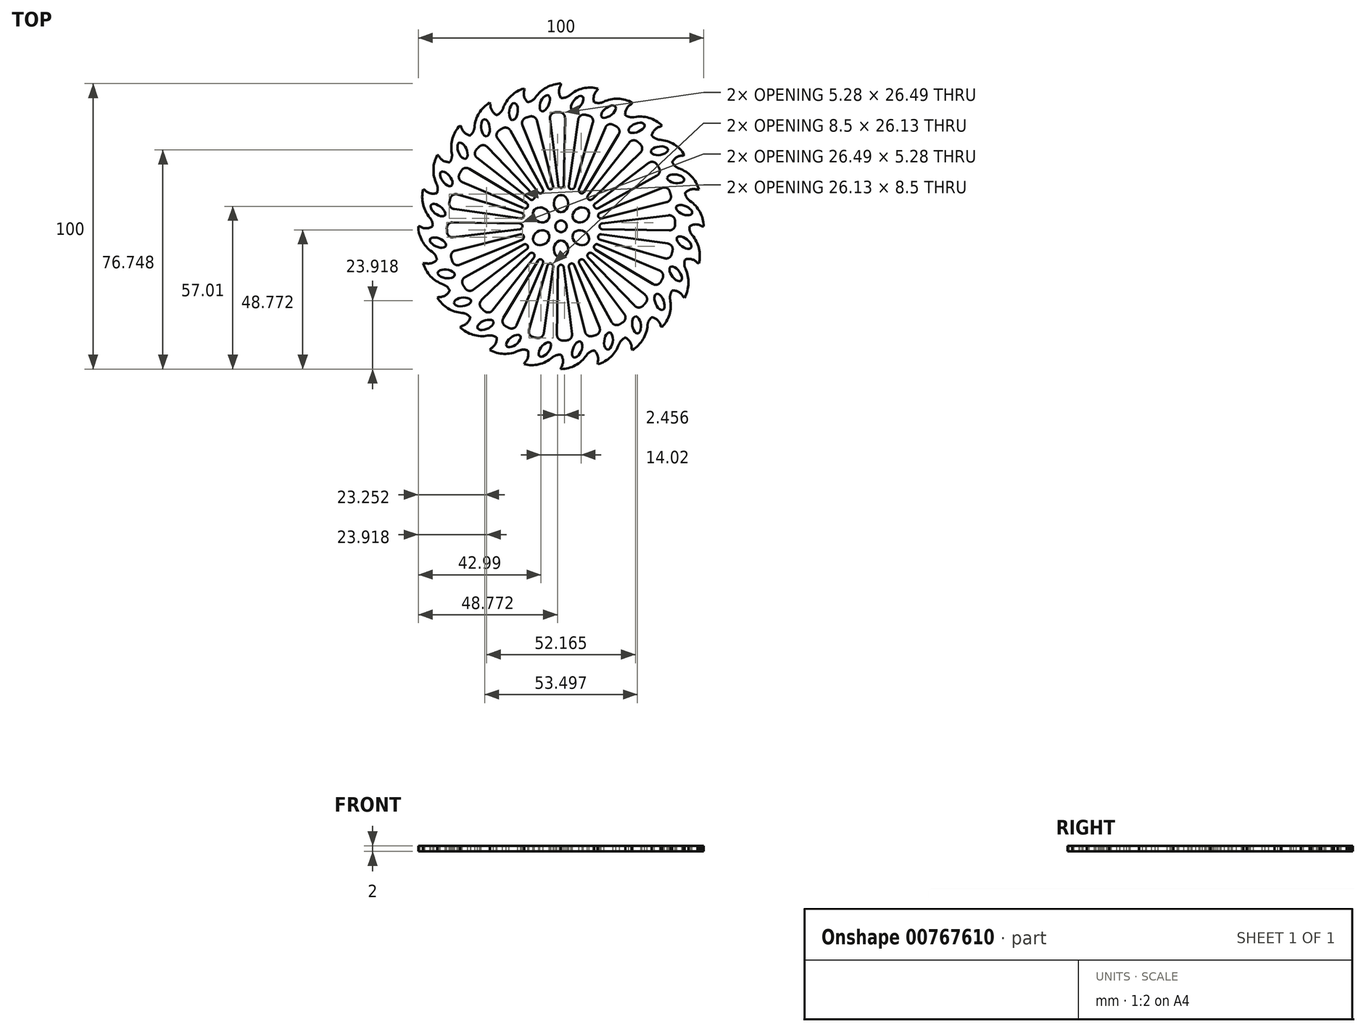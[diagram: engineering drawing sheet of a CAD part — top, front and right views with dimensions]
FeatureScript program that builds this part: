
annotation { "Feature Type Name" : "Feature", "Feature Type Description" : "" }
export const myFeature = defineFeature(function(context is Context, id is Id, definition is map)
    precondition{}
    {
        {
            var Q0;
            Q0=qCreatedBy(makeId("Top.planeOp"),FACE);
            var sketch = newSketch(context, id + "F0", { "sketchPlane" : qUnion([Q0])});
            skCircle(sketch, "E0", {"center": v(0, 0) * mm, "radius": 50 * mm});
            skSolve(sketch);
        }
        {
            var Q0;
            Q0 = qSketchRegion(id + "F0", true);
            extrude(context, id + "F1", {"entities" : qUnion([Q0]), "depth" : 2 * mm, "offsetDistance" : 25 * mm});
        }
        {
            var Q0;
            Q0=qCreatedBy(makeId("Top.planeOp"),FACE);
            var sketch = newSketch(context, id + "F2", { "sketchPlane" : qUnion([Q0])});
            skCircle(sketch, "E1", {"center": v(0, 0) * mm, "radius": 2 * mm});
            skCircle(sketch, "E2", {"center": v(0, 0) * mm, "radius": 45 * mm, "construction": true});
            skLineSegment(sketch, "E3", {"start": v(0, 0) * mm, "end": v(-11.65, 43.47) * mm, "construction": true});
            skArc(sketch, "E4", {"start": v(0, 50) * mm, "mid": v(-5.04, 48.69) * mm, "end": v(-8.91, 45.2) * mm});
            skCircle(sketch, "E5", {"center": v(0, 0) * mm, "radius": 50 * mm, "construction": true});
            skArc(sketch, "E6", {"start": v(-11.65, 43.47) * mm, "mid": v(-11.43, 43.52) * mm, "end": v(-11.22, 43.58) * mm});
            skPoint(sketch, "E7.visualSharp", {"position": v(-9.65, 43.95) * mm});
            skArc(sketch, "E7.filletArc", {"start": v(-11.22, 43.58) * mm, "mid": v(-9.92, 44.18) * mm, "end": v(-8.91, 45.2) * mm});
            skLineSegment(sketch, "E8", {"start": v(0, 50) * mm, "end": v(0, 49.5) * mm});
            skArc(sketch, "E9", {"start": v(0, 49.5) * mm, "mid": v(-0.7, 47.25) * mm, "end": v(0, 45) * mm});
            skArc(sketch, "E10.1.0", {"start": v(-12.94, 48.3) * mm, "mid": v(-17.47, 45.72) * mm, "end": v(-20.3, 41.35) * mm});
            skLineSegment(sketch, "E10.1.1", {"start": v(-12.94, 48.3) * mm, "end": v(-12.81, 47.81) * mm});
            skArc(sketch, "E10.1.2", {"start": v(-12.81, 47.81) * mm, "mid": v(-12.9, 45.46) * mm, "end": v(-11.65, 43.47) * mm});
            skArc(sketch, "E10.1.3", {"start": v(-22.12, 39.19) * mm, "mid": v(-21.02, 40.1) * mm, "end": v(-20.3, 41.35) * mm});
            skArc(sketch, "E10.1.4", {"start": v(-22.5, 38.97) * mm, "mid": v(-22.3, 39.08) * mm, "end": v(-22.12, 39.19) * mm});
            skArc(sketch, "E10.2.0", {"start": v(-25, 43.3) * mm, "mid": v(-28.7, 39.64) * mm, "end": v(-30.32, 34.69) * mm});
            skLineSegment(sketch, "E10.2.1", {"start": v(-25, 43.3) * mm, "end": v(-24.75, 42.87) * mm});
            skArc(sketch, "E10.2.2", {"start": v(-24.75, 42.87) * mm, "mid": v(-24.22, 40.57) * mm, "end": v(-22.5, 38.97) * mm});
            skArc(sketch, "E10.2.3", {"start": v(-31.5, 32.13) * mm, "mid": v(-30.68, 33.3) * mm, "end": v(-30.32, 34.69) * mm});
            skArc(sketch, "E10.2.4", {"start": v(-31.82, 31.82) * mm, "mid": v(-31.66, 31.98) * mm, "end": v(-31.5, 32.13) * mm});
            skArc(sketch, "E10.3.0", {"start": v(-35.36, 35.36) * mm, "mid": v(-38, 30.86) * mm, "end": v(-38.26, 25.66) * mm});
            skLineSegment(sketch, "E10.3.1", {"start": v(-35.36, 35.36) * mm, "end": v(-35, 35) * mm});
            skArc(sketch, "E10.3.2", {"start": v(-35, 35) * mm, "mid": v(-33.9, 32.92) * mm, "end": v(-31.82, 31.82) * mm});
            skArc(sketch, "E10.3.3", {"start": v(-38.75, 22.88) * mm, "mid": v(-38.25, 24.23) * mm, "end": v(-38.26, 25.66) * mm});
            skArc(sketch, "E10.3.4", {"start": v(-38.97, 22.5) * mm, "mid": v(-38.86, 22.7) * mm, "end": v(-38.75, 22.88) * mm});
            skArc(sketch, "E10.4.0", {"start": v(-43.3, 25) * mm, "mid": v(-44.68, 19.98) * mm, "end": v(-43.6, 14.88) * mm});
            skLineSegment(sketch, "E10.4.1", {"start": v(-43.3, 25) * mm, "end": v(-42.87, 24.75) * mm});
            skArc(sketch, "E10.4.2", {"start": v(-42.87, 24.75) * mm, "mid": v(-41.27, 23.03) * mm, "end": v(-38.97, 22.5) * mm});
            skArc(sketch, "E10.4.3", {"start": v(-43.35, 12.07) * mm, "mid": v(-43.22, 13.5) * mm, "end": v(-43.6, 14.88) * mm});
            skArc(sketch, "E10.4.4", {"start": v(-43.47, 11.65) * mm, "mid": v(-43.4, 11.86) * mm, "end": v(-43.35, 12.07) * mm});
            skArc(sketch, "E10.5.0", {"start": v(-48.3, 12.94) * mm, "mid": v(-48.33, 7.73) * mm, "end": v(-45.97, 3.09) * mm});
            skLineSegment(sketch, "E10.5.1", {"start": v(-48.3, 12.94) * mm, "end": v(-47.81, 12.81) * mm});
            skArc(sketch, "E10.5.2", {"start": v(-47.81, 12.81) * mm, "mid": v(-45.82, 11.56) * mm, "end": v(-43.47, 11.65) * mm});
            skArc(sketch, "E10.5.3", {"start": v(-45, 0.44) * mm, "mid": v(-45.24, 1.85) * mm, "end": v(-45.97, 3.09) * mm});
            skArc(sketch, "E10.5.4", {"start": v(-45, 0) * mm, "mid": v(-45, 0.22) * mm, "end": v(-45, 0.44) * mm});
            skArc(sketch, "E10.6.0", {"start": v(-50, 0) * mm, "mid": v(-48.69, -5.04) * mm, "end": v(-45.2, -8.91) * mm});
            skLineSegment(sketch, "E10.6.1", {"start": v(-50, 0) * mm, "end": v(-49.5, 0) * mm});
            skArc(sketch, "E10.6.2", {"start": v(-49.5, 0) * mm, "mid": v(-47.25, -0.7) * mm, "end": v(-45, 0) * mm});
            skArc(sketch, "E10.6.3", {"start": v(-43.58, -11.22) * mm, "mid": v(-44.18, -9.92) * mm, "end": v(-45.2, -8.91) * mm});
            skArc(sketch, "E10.6.4", {"start": v(-43.47, -11.65) * mm, "mid": v(-43.52, -11.43) * mm, "end": v(-43.58, -11.22) * mm});
            skArc(sketch, "E10.7.0", {"start": v(-48.3, -12.94) * mm, "mid": v(-45.72, -17.47) * mm, "end": v(-41.35, -20.3) * mm});
            skLineSegment(sketch, "E10.7.1", {"start": v(-48.3, -12.94) * mm, "end": v(-47.81, -12.81) * mm});
            skArc(sketch, "E10.7.2", {"start": v(-47.81, -12.81) * mm, "mid": v(-45.46, -12.9) * mm, "end": v(-43.47, -11.65) * mm});
            skArc(sketch, "E10.7.3", {"start": v(-39.19, -22.12) * mm, "mid": v(-40.1, -21.02) * mm, "end": v(-41.35, -20.3) * mm});
            skArc(sketch, "E10.7.4", {"start": v(-38.97, -22.5) * mm, "mid": v(-39.08, -22.3) * mm, "end": v(-39.19, -22.12) * mm});
            skArc(sketch, "E10.8.0", {"start": v(-43.3, -25) * mm, "mid": v(-39.64, -28.7) * mm, "end": v(-34.69, -30.32) * mm});
            skLineSegment(sketch, "E10.8.1", {"start": v(-43.3, -25) * mm, "end": v(-42.87, -24.75) * mm});
            skArc(sketch, "E10.8.2", {"start": v(-42.87, -24.75) * mm, "mid": v(-40.57, -24.22) * mm, "end": v(-38.97, -22.5) * mm});
            skArc(sketch, "E10.8.3", {"start": v(-32.13, -31.5) * mm, "mid": v(-33.3, -30.68) * mm, "end": v(-34.69, -30.32) * mm});
            skArc(sketch, "E10.8.4", {"start": v(-31.82, -31.82) * mm, "mid": v(-31.98, -31.66) * mm, "end": v(-32.13, -31.5) * mm});
            skArc(sketch, "E10.9.0", {"start": v(-35.36, -35.36) * mm, "mid": v(-30.86, -38) * mm, "end": v(-25.66, -38.26) * mm});
            skLineSegment(sketch, "E10.9.1", {"start": v(-35.36, -35.36) * mm, "end": v(-35, -35) * mm});
            skArc(sketch, "E10.9.2", {"start": v(-35, -35) * mm, "mid": v(-32.92, -33.9) * mm, "end": v(-31.82, -31.82) * mm});
            skArc(sketch, "E10.9.3", {"start": v(-22.88, -38.75) * mm, "mid": v(-24.23, -38.25) * mm, "end": v(-25.66, -38.26) * mm});
            skArc(sketch, "E10.9.4", {"start": v(-22.5, -38.97) * mm, "mid": v(-22.7, -38.86) * mm, "end": v(-22.88, -38.75) * mm});
            skArc(sketch, "E10.10.0", {"start": v(-25, -43.3) * mm, "mid": v(-19.98, -44.68) * mm, "end": v(-14.88, -43.6) * mm});
            skLineSegment(sketch, "E10.10.1", {"start": v(-25, -43.3) * mm, "end": v(-24.75, -42.87) * mm});
            skArc(sketch, "E10.10.2", {"start": v(-24.75, -42.87) * mm, "mid": v(-23.03, -41.27) * mm, "end": v(-22.5, -38.97) * mm});
            skArc(sketch, "E10.10.3", {"start": v(-12.07, -43.35) * mm, "mid": v(-13.5, -43.22) * mm, "end": v(-14.88, -43.6) * mm});
            skArc(sketch, "E10.10.4", {"start": v(-11.65, -43.47) * mm, "mid": v(-11.86, -43.4) * mm, "end": v(-12.07, -43.35) * mm});
            skArc(sketch, "E10.11.0", {"start": v(-12.94, -48.3) * mm, "mid": v(-7.73, -48.33) * mm, "end": v(-3.09, -45.97) * mm});
            skLineSegment(sketch, "E10.11.1", {"start": v(-12.94, -48.3) * mm, "end": v(-12.81, -47.81) * mm});
            skArc(sketch, "E10.11.2", {"start": v(-12.81, -47.81) * mm, "mid": v(-11.56, -45.82) * mm, "end": v(-11.65, -43.47) * mm});
            skArc(sketch, "E10.11.3", {"start": v(-0.44, -45) * mm, "mid": v(-1.85, -45.24) * mm, "end": v(-3.09, -45.97) * mm});
            skArc(sketch, "E10.11.4", {"start": v(0, -45) * mm, "mid": v(-0.22, -45) * mm, "end": v(-0.44, -45) * mm});
            skArc(sketch, "E10.12.0", {"start": v(0, -50) * mm, "mid": v(5.04, -48.69) * mm, "end": v(8.91, -45.2) * mm});
            skLineSegment(sketch, "E10.12.1", {"start": v(0, -50) * mm, "end": v(0, -49.5) * mm});
            skArc(sketch, "E10.12.2", {"start": v(0, -49.5) * mm, "mid": v(0.7, -47.25) * mm, "end": v(0, -45) * mm});
            skArc(sketch, "E10.12.3", {"start": v(11.22, -43.58) * mm, "mid": v(9.92, -44.18) * mm, "end": v(8.91, -45.2) * mm});
            skArc(sketch, "E10.12.4", {"start": v(11.65, -43.47) * mm, "mid": v(11.43, -43.52) * mm, "end": v(11.22, -43.58) * mm});
            skArc(sketch, "E10.13.0", {"start": v(12.94, -48.3) * mm, "mid": v(17.47, -45.72) * mm, "end": v(20.3, -41.35) * mm});
            skLineSegment(sketch, "E10.13.1", {"start": v(12.94, -48.3) * mm, "end": v(12.81, -47.81) * mm});
            skArc(sketch, "E10.13.2", {"start": v(12.81, -47.81) * mm, "mid": v(12.9, -45.46) * mm, "end": v(11.65, -43.47) * mm});
            skArc(sketch, "E10.13.3", {"start": v(22.12, -39.19) * mm, "mid": v(21.02, -40.1) * mm, "end": v(20.3, -41.35) * mm});
            skArc(sketch, "E10.13.4", {"start": v(22.5, -38.97) * mm, "mid": v(22.3, -39.08) * mm, "end": v(22.12, -39.19) * mm});
            skArc(sketch, "E10.14.0", {"start": v(25, -43.3) * mm, "mid": v(28.7, -39.64) * mm, "end": v(30.32, -34.69) * mm});
            skLineSegment(sketch, "E10.14.1", {"start": v(25, -43.3) * mm, "end": v(24.75, -42.87) * mm});
            skArc(sketch, "E10.14.2", {"start": v(24.75, -42.87) * mm, "mid": v(24.22, -40.57) * mm, "end": v(22.5, -38.97) * mm});
            skArc(sketch, "E10.14.3", {"start": v(31.5, -32.13) * mm, "mid": v(30.68, -33.3) * mm, "end": v(30.32, -34.69) * mm});
            skArc(sketch, "E10.14.4", {"start": v(31.82, -31.82) * mm, "mid": v(31.66, -31.98) * mm, "end": v(31.5, -32.13) * mm});
            skArc(sketch, "E10.15.0", {"start": v(35.36, -35.36) * mm, "mid": v(38, -30.86) * mm, "end": v(38.26, -25.66) * mm});
            skLineSegment(sketch, "E10.15.1", {"start": v(35.36, -35.36) * mm, "end": v(35, -35) * mm});
            skArc(sketch, "E10.15.2", {"start": v(35, -35) * mm, "mid": v(33.9, -32.92) * mm, "end": v(31.82, -31.82) * mm});
            skArc(sketch, "E10.15.3", {"start": v(38.75, -22.88) * mm, "mid": v(38.25, -24.23) * mm, "end": v(38.26, -25.66) * mm});
            skArc(sketch, "E10.15.4", {"start": v(38.97, -22.5) * mm, "mid": v(38.86, -22.7) * mm, "end": v(38.75, -22.88) * mm});
            skArc(sketch, "E10.16.0", {"start": v(43.3, -25) * mm, "mid": v(44.68, -19.98) * mm, "end": v(43.6, -14.88) * mm});
            skLineSegment(sketch, "E10.16.1", {"start": v(43.3, -25) * mm, "end": v(42.87, -24.75) * mm});
            skArc(sketch, "E10.16.2", {"start": v(42.87, -24.75) * mm, "mid": v(41.27, -23.03) * mm, "end": v(38.97, -22.5) * mm});
            skArc(sketch, "E10.16.3", {"start": v(43.35, -12.07) * mm, "mid": v(43.22, -13.5) * mm, "end": v(43.6, -14.88) * mm});
            skArc(sketch, "E10.16.4", {"start": v(43.47, -11.65) * mm, "mid": v(43.4, -11.86) * mm, "end": v(43.35, -12.07) * mm});
            skArc(sketch, "E10.17.0", {"start": v(48.3, -12.94) * mm, "mid": v(48.33, -7.73) * mm, "end": v(45.97, -3.09) * mm});
            skLineSegment(sketch, "E10.17.1", {"start": v(48.3, -12.94) * mm, "end": v(47.81, -12.81) * mm});
            skArc(sketch, "E10.17.2", {"start": v(47.81, -12.81) * mm, "mid": v(45.82, -11.56) * mm, "end": v(43.47, -11.65) * mm});
            skArc(sketch, "E10.17.3", {"start": v(45, -0.44) * mm, "mid": v(45.24, -1.85) * mm, "end": v(45.97, -3.09) * mm});
            skArc(sketch, "E10.17.4", {"start": v(45, 0) * mm, "mid": v(45, -0.22) * mm, "end": v(45, -0.44) * mm});
            skArc(sketch, "E10.18.0", {"start": v(50, 0) * mm, "mid": v(48.69, 5.04) * mm, "end": v(45.2, 8.91) * mm});
            skLineSegment(sketch, "E10.18.1", {"start": v(50, 0) * mm, "end": v(49.5, 0) * mm});
            skArc(sketch, "E10.18.2", {"start": v(49.5, 0) * mm, "mid": v(47.25, 0.7) * mm, "end": v(45, 0) * mm});
            skArc(sketch, "E10.18.3", {"start": v(43.58, 11.22) * mm, "mid": v(44.18, 9.92) * mm, "end": v(45.2, 8.91) * mm});
            skArc(sketch, "E10.18.4", {"start": v(43.47, 11.65) * mm, "mid": v(43.52, 11.43) * mm, "end": v(43.58, 11.22) * mm});
            skArc(sketch, "E10.19.0", {"start": v(48.3, 12.94) * mm, "mid": v(45.72, 17.47) * mm, "end": v(41.35, 20.3) * mm});
            skLineSegment(sketch, "E10.19.1", {"start": v(48.3, 12.94) * mm, "end": v(47.81, 12.81) * mm});
            skArc(sketch, "E10.19.2", {"start": v(47.81, 12.81) * mm, "mid": v(45.46, 12.9) * mm, "end": v(43.47, 11.65) * mm});
            skArc(sketch, "E10.19.3", {"start": v(39.19, 22.12) * mm, "mid": v(40.1, 21.02) * mm, "end": v(41.35, 20.3) * mm});
            skArc(sketch, "E10.19.4", {"start": v(38.97, 22.5) * mm, "mid": v(39.08, 22.3) * mm, "end": v(39.19, 22.12) * mm});
            skArc(sketch, "E10.20.0", {"start": v(43.3, 25) * mm, "mid": v(39.64, 28.7) * mm, "end": v(34.69, 30.32) * mm});
            skLineSegment(sketch, "E10.20.1", {"start": v(43.3, 25) * mm, "end": v(42.87, 24.75) * mm});
            skArc(sketch, "E10.20.2", {"start": v(42.87, 24.75) * mm, "mid": v(40.57, 24.22) * mm, "end": v(38.97, 22.5) * mm});
            skArc(sketch, "E10.20.3", {"start": v(32.13, 31.5) * mm, "mid": v(33.3, 30.68) * mm, "end": v(34.69, 30.32) * mm});
            skArc(sketch, "E10.20.4", {"start": v(31.82, 31.82) * mm, "mid": v(31.98, 31.66) * mm, "end": v(32.13, 31.5) * mm});
            skArc(sketch, "E10.21.0", {"start": v(35.36, 35.36) * mm, "mid": v(30.86, 38) * mm, "end": v(25.66, 38.26) * mm});
            skLineSegment(sketch, "E10.21.1", {"start": v(35.36, 35.36) * mm, "end": v(35, 35) * mm});
            skArc(sketch, "E10.21.2", {"start": v(35, 35) * mm, "mid": v(32.92, 33.9) * mm, "end": v(31.82, 31.82) * mm});
            skArc(sketch, "E10.21.3", {"start": v(22.88, 38.75) * mm, "mid": v(24.23, 38.25) * mm, "end": v(25.66, 38.26) * mm});
            skArc(sketch, "E10.21.4", {"start": v(22.5, 38.97) * mm, "mid": v(22.7, 38.86) * mm, "end": v(22.88, 38.75) * mm});
            skArc(sketch, "E10.22.0", {"start": v(25, 43.3) * mm, "mid": v(19.98, 44.68) * mm, "end": v(14.88, 43.6) * mm});
            skLineSegment(sketch, "E10.22.1", {"start": v(25, 43.3) * mm, "end": v(24.75, 42.87) * mm});
            skArc(sketch, "E10.22.2", {"start": v(24.75, 42.87) * mm, "mid": v(23.03, 41.27) * mm, "end": v(22.5, 38.97) * mm});
            skArc(sketch, "E10.22.3", {"start": v(12.07, 43.35) * mm, "mid": v(13.5, 43.22) * mm, "end": v(14.88, 43.6) * mm});
            skArc(sketch, "E10.22.4", {"start": v(11.65, 43.47) * mm, "mid": v(11.86, 43.4) * mm, "end": v(12.07, 43.35) * mm});
            skArc(sketch, "E10.23.0", {"start": v(12.94, 48.3) * mm, "mid": v(7.73, 48.33) * mm, "end": v(3.09, 45.97) * mm});
            skLineSegment(sketch, "E10.23.1", {"start": v(12.94, 48.3) * mm, "end": v(12.81, 47.81) * mm});
            skArc(sketch, "E10.23.2", {"start": v(12.81, 47.81) * mm, "mid": v(11.56, 45.82) * mm, "end": v(11.65, 43.47) * mm});
            skArc(sketch, "E10.23.3", {"start": v(0.44, 45) * mm, "mid": v(1.85, 45.24) * mm, "end": v(3.09, 45.97) * mm});
            skArc(sketch, "E10.23.4", {"start": v(0, 45) * mm, "mid": v(0.22, 45) * mm, "end": v(0.44, 45) * mm});
            skSolve(sketch);
        }
        {
            var Q0;
            Q0 = qSketchRegion(id + "F2", true);
            extrude(context, id + "F3", {"entities" : qUnion([Q0]), "operationType" : NewBodyOperationType.ADD, "depth" : 4 * mm, "offsetDistance" : 25 * mm});
        }
        {
            var Q0;
            Q0=makeQuery(id+"F1.opExtrude","CAP_FACE",FACE,{"disambiguationData":[OSD([sQuery(id+"F0.wireOp",EDGE,"E0")])],"isStart":true});
            var sketch = newSketch(context, id + "F4", { "sketchPlane" : qUnion([Q0])});
            skCircle(sketch, "E11", {"center": v(0, 0) * mm, "radius": 50 * mm});
            skSolve(sketch);
        }
        {
            var Q0;
            Q0 = qSketchRegion(id + "F4", true);
            extrude(context, id + "F5", {"entities" : qUnion([Q0]), "operationType" : NewBodyOperationType.REMOVE, "oppositeDirection" : true, "depth" : 2 * mm, "offsetDistance" : 25 * mm});
        }
        {
            var Q0;
            Q0=makeQuery(id+"F3.opExtrude","CAP_FACE",FACE,{"disambiguationData":[OSD([sQuery(id+"F2.wireOp",EDGE,"E1"),sQuery(id+"F2.wireOp",EDGE,"E4"),sQuery(id+"F2.wireOp",EDGE,"E8"),sQuery(id+"F2.wireOp",EDGE,"E9"),sQuery(id+"F2.wireOp",EDGE,"E7.filletArc"),sQuery(id+"F2.wireOp",EDGE,"E6"),sQuery(id+"F2.wireOp",EDGE,"E10.1.0"),sQuery(id+"F2.wireOp",EDGE,"E10.1.1"),sQuery(id+"F2.wireOp",EDGE,"E10.1.2"),sQuery(id+"F2.wireOp",EDGE,"E10.1.3"),sQuery(id+"F2.wireOp",EDGE,"E10.1.4"),sQuery(id+"F2.wireOp",EDGE,"E10.2.0"),sQuery(id+"F2.wireOp",EDGE,"E10.2.1"),sQuery(id+"F2.wireOp",EDGE,"E10.2.2"),sQuery(id+"F2.wireOp",EDGE,"E10.2.3"),sQuery(id+"F2.wireOp",EDGE,"E10.2.4"),sQuery(id+"F2.wireOp",EDGE,"E10.3.0"),sQuery(id+"F2.wireOp",EDGE,"E10.3.1"),sQuery(id+"F2.wireOp",EDGE,"E10.3.2"),sQuery(id+"F2.wireOp",EDGE,"E10.3.3"),sQuery(id+"F2.wireOp",EDGE,"E10.3.4"),sQuery(id+"F2.wireOp",EDGE,"E10.4.0"),sQuery(id+"F2.wireOp",EDGE,"E10.4.1"),sQuery(id+"F2.wireOp",EDGE,"E10.4.2"),sQuery(id+"F2.wireOp",EDGE,"E10.4.3"),sQuery(id+"F2.wireOp",EDGE,"E10.4.4"),sQuery(id+"F2.wireOp",EDGE,"E10.5.0"),sQuery(id+"F2.wireOp",EDGE,"E10.5.1"),sQuery(id+"F2.wireOp",EDGE,"E10.5.2"),sQuery(id+"F2.wireOp",EDGE,"E10.5.3"),sQuery(id+"F2.wireOp",EDGE,"E10.5.4"),sQuery(id+"F2.wireOp",EDGE,"E10.6.0"),sQuery(id+"F2.wireOp",EDGE,"E10.6.1"),sQuery(id+"F2.wireOp",EDGE,"E10.6.2"),sQuery(id+"F2.wireOp",EDGE,"E10.6.3"),sQuery(id+"F2.wireOp",EDGE,"E10.6.4"),sQuery(id+"F2.wireOp",EDGE,"E10.7.0"),sQuery(id+"F2.wireOp",EDGE,"E10.7.1"),sQuery(id+"F2.wireOp",EDGE,"E10.7.2"),sQuery(id+"F2.wireOp",EDGE,"E10.7.3"),sQuery(id+"F2.wireOp",EDGE,"E10.7.4"),sQuery(id+"F2.wireOp",EDGE,"E10.8.0"),sQuery(id+"F2.wireOp",EDGE,"E10.8.1"),sQuery(id+"F2.wireOp",EDGE,"E10.8.2"),sQuery(id+"F2.wireOp",EDGE,"E10.8.3"),sQuery(id+"F2.wireOp",EDGE,"E10.8.4"),sQuery(id+"F2.wireOp",EDGE,"E10.9.0"),sQuery(id+"F2.wireOp",EDGE,"E10.9.1"),sQuery(id+"F2.wireOp",EDGE,"E10.9.2"),sQuery(id+"F2.wireOp",EDGE,"E10.9.3"),sQuery(id+"F2.wireOp",EDGE,"E10.9.4"),sQuery(id+"F2.wireOp",EDGE,"E10.10.0"),sQuery(id+"F2.wireOp",EDGE,"E10.10.1"),sQuery(id+"F2.wireOp",EDGE,"E10.10.2"),sQuery(id+"F2.wireOp",EDGE,"E10.10.3"),sQuery(id+"F2.wireOp",EDGE,"E10.10.4"),sQuery(id+"F2.wireOp",EDGE,"E10.11.0"),sQuery(id+"F2.wireOp",EDGE,"E10.11.1"),sQuery(id+"F2.wireOp",EDGE,"E10.11.2"),sQuery(id+"F2.wireOp",EDGE,"E10.11.3"),sQuery(id+"F2.wireOp",EDGE,"E10.11.4"),sQuery(id+"F2.wireOp",EDGE,"E10.12.0"),sQuery(id+"F2.wireOp",EDGE,"E10.12.1"),sQuery(id+"F2.wireOp",EDGE,"E10.12.2"),sQuery(id+"F2.wireOp",EDGE,"E10.12.3"),sQuery(id+"F2.wireOp",EDGE,"E10.12.4"),sQuery(id+"F2.wireOp",EDGE,"E10.13.0"),sQuery(id+"F2.wireOp",EDGE,"E10.13.1"),sQuery(id+"F2.wireOp",EDGE,"E10.13.2"),sQuery(id+"F2.wireOp",EDGE,"E10.13.3"),sQuery(id+"F2.wireOp",EDGE,"E10.13.4"),sQuery(id+"F2.wireOp",EDGE,"E10.14.0"),sQuery(id+"F2.wireOp",EDGE,"E10.14.1"),sQuery(id+"F2.wireOp",EDGE,"E10.14.2"),sQuery(id+"F2.wireOp",EDGE,"E10.14.3"),sQuery(id+"F2.wireOp",EDGE,"E10.14.4"),sQuery(id+"F2.wireOp",EDGE,"E10.15.0"),sQuery(id+"F2.wireOp",EDGE,"E10.15.1"),sQuery(id+"F2.wireOp",EDGE,"E10.15.2"),sQuery(id+"F2.wireOp",EDGE,"E10.15.3"),sQuery(id+"F2.wireOp",EDGE,"E10.15.4"),sQuery(id+"F2.wireOp",EDGE,"E10.16.0"),sQuery(id+"F2.wireOp",EDGE,"E10.16.1"),sQuery(id+"F2.wireOp",EDGE,"E10.16.2"),sQuery(id+"F2.wireOp",EDGE,"E10.16.3"),sQuery(id+"F2.wireOp",EDGE,"E10.16.4"),sQuery(id+"F2.wireOp",EDGE,"E10.17.0"),sQuery(id+"F2.wireOp",EDGE,"E10.17.1"),sQuery(id+"F2.wireOp",EDGE,"E10.17.2"),sQuery(id+"F2.wireOp",EDGE,"E10.17.3"),sQuery(id+"F2.wireOp",EDGE,"E10.17.4"),sQuery(id+"F2.wireOp",EDGE,"E10.18.0"),sQuery(id+"F2.wireOp",EDGE,"E10.18.1"),sQuery(id+"F2.wireOp",EDGE,"E10.18.2"),sQuery(id+"F2.wireOp",EDGE,"E10.18.3"),sQuery(id+"F2.wireOp",EDGE,"E10.18.4"),sQuery(id+"F2.wireOp",EDGE,"E10.19.0"),sQuery(id+"F2.wireOp",EDGE,"E10.19.1"),sQuery(id+"F2.wireOp",EDGE,"E10.19.2"),sQuery(id+"F2.wireOp",EDGE,"E10.19.3"),sQuery(id+"F2.wireOp",EDGE,"E10.19.4"),sQuery(id+"F2.wireOp",EDGE,"E10.20.0"),sQuery(id+"F2.wireOp",EDGE,"E10.20.1"),sQuery(id+"F2.wireOp",EDGE,"E10.20.2"),sQuery(id+"F2.wireOp",EDGE,"E10.20.3"),sQuery(id+"F2.wireOp",EDGE,"E10.20.4"),sQuery(id+"F2.wireOp",EDGE,"E10.21.0"),sQuery(id+"F2.wireOp",EDGE,"E10.21.1"),sQuery(id+"F2.wireOp",EDGE,"E10.21.2"),sQuery(id+"F2.wireOp",EDGE,"E10.21.3"),sQuery(id+"F2.wireOp",EDGE,"E10.21.4"),sQuery(id+"F2.wireOp",EDGE,"E10.22.0"),sQuery(id+"F2.wireOp",EDGE,"E10.22.1"),sQuery(id+"F2.wireOp",EDGE,"E10.22.2"),sQuery(id+"F2.wireOp",EDGE,"E10.22.3"),sQuery(id+"F2.wireOp",EDGE,"E10.22.4"),sQuery(id+"F2.wireOp",EDGE,"E10.23.0"),sQuery(id+"F2.wireOp",EDGE,"E10.23.1"),sQuery(id+"F2.wireOp",EDGE,"E10.23.2"),sQuery(id+"F2.wireOp",EDGE,"E10.23.3"),sQuery(id+"F2.wireOp",EDGE,"E10.23.4")])],"isStart":false});
            var sketch = newSketch(context, id + "F6", { "sketchPlane" : qUnion([Q0])});
            skLineSegment(sketch, "E12", {"start": v(-3.86, 37.71) * mm, "end": v(-1, 14.38) * mm});
            skLineSegment(sketch, "E13", {"start": v(1, 14.48) * mm, "end": v(1.4, 37.96) * mm});
            skArc(sketch, "E14.filletArc", {"start": v(-1, 14.38) * mm, "mid": v(0.05, 13.5) * mm, "end": v(1, 14.48) * mm});
            skPoint(sketch, "E15.visualSharp", {"position": v(-4.25, 40.9) * mm});
            skPoint(sketch, "E16.visualSharp", {"position": v(1.47, 41.18) * mm});
            skArc(sketch, "E17", {"start": v(-1.97, 39.95) * mm, "mid": v(-3.4, 39.24) * mm, "end": v(-3.86, 37.71) * mm});
            skArc(sketch, "E18", {"start": v(1.4, 37.96) * mm, "mid": v(0.83, 39.4) * mm, "end": v(-0.62, 40) * mm});
            skArc(sketch, "E19", {"start": v(-1.97, 39.95) * mm, "mid": v(-1.3, 39.98) * mm, "end": v(-0.62, 40) * mm});
            skArc(sketch, "E20.1.0", {"start": v(-12.24, 38.08) * mm, "mid": v(-13.44, 37.02) * mm, "end": v(-13.49, 35.43) * mm});
            skArc(sketch, "E20.1.1", {"start": v(-12.24, 38.08) * mm, "mid": v(-11.6, 38.28) * mm, "end": v(-10.95, 38.47) * mm});
            skArc(sketch, "E20.1.2", {"start": v(-8.46, 37.03) * mm, "mid": v(-9.4, 38.28) * mm, "end": v(-10.95, 38.47) * mm});
            skLineSegment(sketch, "E20.1.3", {"start": v(-2.78, 14.25) * mm, "end": v(-8.46, 37.03) * mm});
            skLineSegment(sketch, "E20.1.4", {"start": v(-13.49, 35.43) * mm, "end": v(-4.68, 13.63) * mm});
            skArc(sketch, "E20.1.5", {"start": v(-4.68, 13.63) * mm, "mid": v(-3.44, 13.05) * mm, "end": v(-2.78, 14.25) * mm});
            skArc(sketch, "E20.2.0", {"start": v(-21.68, 33.61) * mm, "mid": v(-22.57, 32.28) * mm, "end": v(-22.2, 30.73) * mm});
            skArc(sketch, "E20.2.1", {"start": v(-21.68, 33.61) * mm, "mid": v(-21.11, 33.97) * mm, "end": v(-20.54, 34.33) * mm});
            skArc(sketch, "E20.2.2", {"start": v(-17.76, 33.58) * mm, "mid": v(-18.99, 34.54) * mm, "end": v(-20.54, 34.33) * mm});
            skLineSegment(sketch, "E20.2.3", {"start": v(-6.38, 13.04) * mm, "end": v(-17.76, 33.58) * mm});
            skLineSegment(sketch, "E20.2.4", {"start": v(-22.2, 30.73) * mm, "end": v(-8.05, 11.96) * mm});
            skArc(sketch, "E20.2.5", {"start": v(-8.05, 11.96) * mm, "mid": v(-6.7, 11.72) * mm, "end": v(-6.38, 13.04) * mm});
            skArc(sketch, "E20.3.0", {"start": v(-29.64, 26.86) * mm, "mid": v(-30.15, 25.34) * mm, "end": v(-29.4, 23.94) * mm});
            skArc(sketch, "E20.3.1", {"start": v(-29.64, 26.86) * mm, "mid": v(-29.19, 27.35) * mm, "end": v(-28.72, 27.84) * mm});
            skArc(sketch, "E20.3.2", {"start": v(-25.85, 27.84) * mm, "mid": v(-27.28, 28.45) * mm, "end": v(-28.72, 27.84) * mm});
            skLineSegment(sketch, "E20.3.3", {"start": v(-9.53, 10.95) * mm, "end": v(-25.85, 27.84) * mm});
            skLineSegment(sketch, "E20.3.4", {"start": v(-29.4, 23.94) * mm, "end": v(-10.87, 9.47) * mm});
            skArc(sketch, "E20.3.5", {"start": v(-10.87, 9.47) * mm, "mid": v(-9.5, 9.58) * mm, "end": v(-9.53, 10.95) * mm});
            skArc(sketch, "E20.4.0", {"start": v(-35.58, 18.27) * mm, "mid": v(-35.69, 16.67) * mm, "end": v(-34.59, 15.51) * mm});
            skArc(sketch, "E20.4.1", {"start": v(-35.58, 18.27) * mm, "mid": v(-35.27, 18.87) * mm, "end": v(-34.95, 19.46) * mm});
            skArc(sketch, "E20.4.2", {"start": v(-32.17, 20.2) * mm, "mid": v(-33.72, 20.42) * mm, "end": v(-34.95, 19.46) * mm});
            skLineSegment(sketch, "E20.4.3", {"start": v(-12.04, 8.1) * mm, "end": v(-32.17, 20.2) * mm});
            skLineSegment(sketch, "E20.4.4", {"start": v(-34.59, 15.51) * mm, "end": v(-12.95, 6.33) * mm});
            skArc(sketch, "E20.4.5", {"start": v(-12.95, 6.33) * mm, "mid": v(-11.67, 6.8) * mm, "end": v(-12.04, 8.1) * mm});
            skArc(sketch, "E20.5.0", {"start": v(-39.1, 8.44) * mm, "mid": v(-38.79, 6.87) * mm, "end": v(-37.42, 6.03) * mm});
            skArc(sketch, "E20.5.1", {"start": v(-39.1, 8.44) * mm, "mid": v(-38.95, 9.1) * mm, "end": v(-38.8, 9.75) * mm});
            skArc(sketch, "E20.5.2", {"start": v(-36.3, 11.19) * mm, "mid": v(-37.85, 11) * mm, "end": v(-38.8, 9.75) * mm});
            skLineSegment(sketch, "E20.5.3", {"start": v(-13.73, 4.71) * mm, "end": v(-36.3, 11.19) * mm});
            skLineSegment(sketch, "E20.5.4", {"start": v(-37.42, 6.03) * mm, "end": v(-14.15, 2.76) * mm});
            skArc(sketch, "E20.5.5", {"start": v(-14.15, 2.76) * mm, "mid": v(-13.03, 3.54) * mm, "end": v(-13.73, 4.71) * mm});
            skArc(sketch, "E20.6.0", {"start": v(-39.95, -1.97) * mm, "mid": v(-39.24, -3.4) * mm, "end": v(-37.71, -3.86) * mm});
            skArc(sketch, "E20.6.1", {"start": v(-39.95, -1.97) * mm, "mid": v(-39.98, -1.3) * mm, "end": v(-40, -0.62) * mm});
            skArc(sketch, "E20.6.2", {"start": v(-37.96, 1.4) * mm, "mid": v(-39.4, 0.83) * mm, "end": v(-40, -0.62) * mm});
            skLineSegment(sketch, "E20.6.3", {"start": v(-14.48, 1) * mm, "end": v(-37.96, 1.4) * mm});
            skLineSegment(sketch, "E20.6.4", {"start": v(-37.71, -3.86) * mm, "end": v(-14.38, -1) * mm});
            skArc(sketch, "E20.6.5", {"start": v(-14.38, -1) * mm, "mid": v(-13.5, 0.05) * mm, "end": v(-14.48, 1) * mm});
            skArc(sketch, "E20.7.0", {"start": v(-38.08, -12.24) * mm, "mid": v(-37.02, -13.44) * mm, "end": v(-35.43, -13.49) * mm});
            skArc(sketch, "E20.7.1", {"start": v(-38.08, -12.24) * mm, "mid": v(-38.28, -11.6) * mm, "end": v(-38.47, -10.95) * mm});
            skArc(sketch, "E20.7.2", {"start": v(-37.03, -8.46) * mm, "mid": v(-38.28, -9.4) * mm, "end": v(-38.47, -10.95) * mm});
            skLineSegment(sketch, "E20.7.3", {"start": v(-14.25, -2.78) * mm, "end": v(-37.03, -8.46) * mm});
            skLineSegment(sketch, "E20.7.4", {"start": v(-35.43, -13.49) * mm, "end": v(-13.63, -4.68) * mm});
            skArc(sketch, "E20.7.5", {"start": v(-13.63, -4.68) * mm, "mid": v(-13.05, -3.44) * mm, "end": v(-14.25, -2.78) * mm});
            skArc(sketch, "E20.8.0", {"start": v(-33.61, -21.68) * mm, "mid": v(-32.28, -22.57) * mm, "end": v(-30.73, -22.2) * mm});
            skArc(sketch, "E20.8.1", {"start": v(-33.61, -21.68) * mm, "mid": v(-33.97, -21.11) * mm, "end": v(-34.33, -20.54) * mm});
            skArc(sketch, "E20.8.2", {"start": v(-33.58, -17.76) * mm, "mid": v(-34.54, -18.99) * mm, "end": v(-34.33, -20.54) * mm});
            skLineSegment(sketch, "E20.8.3", {"start": v(-13.04, -6.38) * mm, "end": v(-33.58, -17.76) * mm});
            skLineSegment(sketch, "E20.8.4", {"start": v(-30.73, -22.2) * mm, "end": v(-11.96, -8.05) * mm});
            skArc(sketch, "E20.8.5", {"start": v(-11.96, -8.05) * mm, "mid": v(-11.72, -6.7) * mm, "end": v(-13.04, -6.38) * mm});
            skArc(sketch, "E20.9.0", {"start": v(-26.86, -29.64) * mm, "mid": v(-25.34, -30.15) * mm, "end": v(-23.94, -29.4) * mm});
            skArc(sketch, "E20.9.1", {"start": v(-26.86, -29.64) * mm, "mid": v(-27.35, -29.19) * mm, "end": v(-27.84, -28.72) * mm});
            skArc(sketch, "E20.9.2", {"start": v(-27.84, -25.85) * mm, "mid": v(-28.45, -27.28) * mm, "end": v(-27.84, -28.72) * mm});
            skLineSegment(sketch, "E20.9.3", {"start": v(-10.95, -9.53) * mm, "end": v(-27.84, -25.85) * mm});
            skLineSegment(sketch, "E20.9.4", {"start": v(-23.94, -29.4) * mm, "end": v(-9.47, -10.87) * mm});
            skArc(sketch, "E20.9.5", {"start": v(-9.47, -10.87) * mm, "mid": v(-9.58, -9.5) * mm, "end": v(-10.95, -9.53) * mm});
            skArc(sketch, "E20.10.0", {"start": v(-18.27, -35.58) * mm, "mid": v(-16.67, -35.69) * mm, "end": v(-15.51, -34.59) * mm});
            skArc(sketch, "E20.10.1", {"start": v(-18.27, -35.58) * mm, "mid": v(-18.87, -35.27) * mm, "end": v(-19.46, -34.95) * mm});
            skArc(sketch, "E20.10.2", {"start": v(-20.2, -32.17) * mm, "mid": v(-20.42, -33.72) * mm, "end": v(-19.46, -34.95) * mm});
            skLineSegment(sketch, "E20.10.3", {"start": v(-8.1, -12.04) * mm, "end": v(-20.2, -32.17) * mm});
            skLineSegment(sketch, "E20.10.4", {"start": v(-15.51, -34.59) * mm, "end": v(-6.33, -12.95) * mm});
            skArc(sketch, "E20.10.5", {"start": v(-6.33, -12.95) * mm, "mid": v(-6.8, -11.67) * mm, "end": v(-8.1, -12.04) * mm});
            skArc(sketch, "E20.11.0", {"start": v(-8.44, -39.1) * mm, "mid": v(-6.87, -38.79) * mm, "end": v(-6.03, -37.42) * mm});
            skArc(sketch, "E20.11.1", {"start": v(-8.44, -39.1) * mm, "mid": v(-9.1, -38.95) * mm, "end": v(-9.75, -38.8) * mm});
            skArc(sketch, "E20.11.2", {"start": v(-11.19, -36.3) * mm, "mid": v(-11, -37.85) * mm, "end": v(-9.75, -38.8) * mm});
            skLineSegment(sketch, "E20.11.3", {"start": v(-4.71, -13.73) * mm, "end": v(-11.19, -36.3) * mm});
            skLineSegment(sketch, "E20.11.4", {"start": v(-6.03, -37.42) * mm, "end": v(-2.76, -14.15) * mm});
            skArc(sketch, "E20.11.5", {"start": v(-2.76, -14.15) * mm, "mid": v(-3.54, -13.03) * mm, "end": v(-4.71, -13.73) * mm});
            skArc(sketch, "E20.12.0", {"start": v(1.97, -39.95) * mm, "mid": v(3.4, -39.24) * mm, "end": v(3.86, -37.71) * mm});
            skArc(sketch, "E20.12.1", {"start": v(1.97, -39.95) * mm, "mid": v(1.3, -39.98) * mm, "end": v(0.62, -40) * mm});
            skArc(sketch, "E20.12.2", {"start": v(-1.4, -37.96) * mm, "mid": v(-0.83, -39.4) * mm, "end": v(0.62, -40) * mm});
            skLineSegment(sketch, "E20.12.3", {"start": v(-1, -14.48) * mm, "end": v(-1.4, -37.96) * mm});
            skLineSegment(sketch, "E20.12.4", {"start": v(3.86, -37.71) * mm, "end": v(1, -14.38) * mm});
            skArc(sketch, "E20.12.5", {"start": v(1, -14.38) * mm, "mid": v(-0.05, -13.5) * mm, "end": v(-1, -14.48) * mm});
            skArc(sketch, "E20.13.0", {"start": v(12.24, -38.08) * mm, "mid": v(13.44, -37.02) * mm, "end": v(13.49, -35.43) * mm});
            skArc(sketch, "E20.13.1", {"start": v(12.24, -38.08) * mm, "mid": v(11.6, -38.28) * mm, "end": v(10.95, -38.47) * mm});
            skArc(sketch, "E20.13.2", {"start": v(8.46, -37.03) * mm, "mid": v(9.4, -38.28) * mm, "end": v(10.95, -38.47) * mm});
            skLineSegment(sketch, "E20.13.3", {"start": v(2.78, -14.25) * mm, "end": v(8.46, -37.03) * mm});
            skLineSegment(sketch, "E20.13.4", {"start": v(13.49, -35.43) * mm, "end": v(4.68, -13.63) * mm});
            skArc(sketch, "E20.13.5", {"start": v(4.68, -13.63) * mm, "mid": v(3.44, -13.05) * mm, "end": v(2.78, -14.25) * mm});
            skArc(sketch, "E20.14.0", {"start": v(21.68, -33.61) * mm, "mid": v(22.57, -32.28) * mm, "end": v(22.2, -30.73) * mm});
            skArc(sketch, "E20.14.1", {"start": v(21.68, -33.61) * mm, "mid": v(21.11, -33.97) * mm, "end": v(20.54, -34.33) * mm});
            skArc(sketch, "E20.14.2", {"start": v(17.76, -33.58) * mm, "mid": v(18.99, -34.54) * mm, "end": v(20.54, -34.33) * mm});
            skLineSegment(sketch, "E20.14.3", {"start": v(6.38, -13.04) * mm, "end": v(17.76, -33.58) * mm});
            skLineSegment(sketch, "E20.14.4", {"start": v(22.2, -30.73) * mm, "end": v(8.05, -11.96) * mm});
            skArc(sketch, "E20.14.5", {"start": v(8.05, -11.96) * mm, "mid": v(6.7, -11.72) * mm, "end": v(6.38, -13.04) * mm});
            skArc(sketch, "E20.15.0", {"start": v(29.64, -26.86) * mm, "mid": v(30.15, -25.34) * mm, "end": v(29.4, -23.94) * mm});
            skArc(sketch, "E20.15.1", {"start": v(29.64, -26.86) * mm, "mid": v(29.19, -27.35) * mm, "end": v(28.72, -27.84) * mm});
            skArc(sketch, "E20.15.2", {"start": v(25.85, -27.84) * mm, "mid": v(27.28, -28.45) * mm, "end": v(28.72, -27.84) * mm});
            skLineSegment(sketch, "E20.15.3", {"start": v(9.53, -10.95) * mm, "end": v(25.85, -27.84) * mm});
            skLineSegment(sketch, "E20.15.4", {"start": v(29.4, -23.94) * mm, "end": v(10.87, -9.47) * mm});
            skArc(sketch, "E20.15.5", {"start": v(10.87, -9.47) * mm, "mid": v(9.5, -9.58) * mm, "end": v(9.53, -10.95) * mm});
            skArc(sketch, "E20.16.0", {"start": v(35.58, -18.27) * mm, "mid": v(35.69, -16.67) * mm, "end": v(34.59, -15.51) * mm});
            skArc(sketch, "E20.16.1", {"start": v(35.58, -18.27) * mm, "mid": v(35.27, -18.87) * mm, "end": v(34.95, -19.46) * mm});
            skArc(sketch, "E20.16.2", {"start": v(32.17, -20.2) * mm, "mid": v(33.72, -20.42) * mm, "end": v(34.95, -19.46) * mm});
            skLineSegment(sketch, "E20.16.3", {"start": v(12.04, -8.1) * mm, "end": v(32.17, -20.2) * mm});
            skLineSegment(sketch, "E20.16.4", {"start": v(34.59, -15.51) * mm, "end": v(12.95, -6.33) * mm});
            skArc(sketch, "E20.16.5", {"start": v(12.95, -6.33) * mm, "mid": v(11.67, -6.8) * mm, "end": v(12.04, -8.1) * mm});
            skArc(sketch, "E20.17.0", {"start": v(39.1, -8.44) * mm, "mid": v(38.79, -6.87) * mm, "end": v(37.42, -6.03) * mm});
            skArc(sketch, "E20.17.1", {"start": v(39.1, -8.44) * mm, "mid": v(38.95, -9.1) * mm, "end": v(38.8, -9.75) * mm});
            skArc(sketch, "E20.17.2", {"start": v(36.3, -11.19) * mm, "mid": v(37.85, -11) * mm, "end": v(38.8, -9.75) * mm});
            skLineSegment(sketch, "E20.17.3", {"start": v(13.73, -4.71) * mm, "end": v(36.3, -11.19) * mm});
            skLineSegment(sketch, "E20.17.4", {"start": v(37.42, -6.03) * mm, "end": v(14.15, -2.76) * mm});
            skArc(sketch, "E20.17.5", {"start": v(14.15, -2.76) * mm, "mid": v(13.03, -3.54) * mm, "end": v(13.73, -4.71) * mm});
            skArc(sketch, "E20.18.0", {"start": v(39.95, 1.97) * mm, "mid": v(39.24, 3.4) * mm, "end": v(37.71, 3.86) * mm});
            skArc(sketch, "E20.18.1", {"start": v(39.95, 1.97) * mm, "mid": v(39.98, 1.3) * mm, "end": v(40, 0.62) * mm});
            skArc(sketch, "E20.18.2", {"start": v(37.96, -1.4) * mm, "mid": v(39.4, -0.83) * mm, "end": v(40, 0.62) * mm});
            skLineSegment(sketch, "E20.18.3", {"start": v(14.48, -1) * mm, "end": v(37.96, -1.4) * mm});
            skLineSegment(sketch, "E20.18.4", {"start": v(37.71, 3.86) * mm, "end": v(14.38, 1) * mm});
            skArc(sketch, "E20.18.5", {"start": v(14.38, 1) * mm, "mid": v(13.5, -0.05) * mm, "end": v(14.48, -1) * mm});
            skArc(sketch, "E20.19.0", {"start": v(38.08, 12.24) * mm, "mid": v(37.02, 13.44) * mm, "end": v(35.43, 13.49) * mm});
            skArc(sketch, "E20.19.1", {"start": v(38.08, 12.24) * mm, "mid": v(38.28, 11.6) * mm, "end": v(38.47, 10.95) * mm});
            skArc(sketch, "E20.19.2", {"start": v(37.03, 8.46) * mm, "mid": v(38.28, 9.4) * mm, "end": v(38.47, 10.95) * mm});
            skLineSegment(sketch, "E20.19.3", {"start": v(14.25, 2.78) * mm, "end": v(37.03, 8.46) * mm});
            skLineSegment(sketch, "E20.19.4", {"start": v(35.43, 13.49) * mm, "end": v(13.63, 4.68) * mm});
            skArc(sketch, "E20.19.5", {"start": v(13.63, 4.68) * mm, "mid": v(13.05, 3.44) * mm, "end": v(14.25, 2.78) * mm});
            skArc(sketch, "E20.20.0", {"start": v(33.61, 21.68) * mm, "mid": v(32.28, 22.57) * mm, "end": v(30.73, 22.2) * mm});
            skArc(sketch, "E20.20.1", {"start": v(33.61, 21.68) * mm, "mid": v(33.97, 21.11) * mm, "end": v(34.33, 20.54) * mm});
            skArc(sketch, "E20.20.2", {"start": v(33.58, 17.76) * mm, "mid": v(34.54, 18.99) * mm, "end": v(34.33, 20.54) * mm});
            skLineSegment(sketch, "E20.20.3", {"start": v(13.04, 6.38) * mm, "end": v(33.58, 17.76) * mm});
            skLineSegment(sketch, "E20.20.4", {"start": v(30.73, 22.2) * mm, "end": v(11.96, 8.05) * mm});
            skArc(sketch, "E20.20.5", {"start": v(11.96, 8.05) * mm, "mid": v(11.72, 6.7) * mm, "end": v(13.04, 6.38) * mm});
            skArc(sketch, "E20.21.0", {"start": v(26.86, 29.64) * mm, "mid": v(25.34, 30.15) * mm, "end": v(23.94, 29.4) * mm});
            skArc(sketch, "E20.21.1", {"start": v(26.86, 29.64) * mm, "mid": v(27.35, 29.19) * mm, "end": v(27.84, 28.72) * mm});
            skArc(sketch, "E20.21.2", {"start": v(27.84, 25.85) * mm, "mid": v(28.45, 27.28) * mm, "end": v(27.84, 28.72) * mm});
            skLineSegment(sketch, "E20.21.3", {"start": v(10.95, 9.53) * mm, "end": v(27.84, 25.85) * mm});
            skLineSegment(sketch, "E20.21.4", {"start": v(23.94, 29.4) * mm, "end": v(9.47, 10.87) * mm});
            skArc(sketch, "E20.21.5", {"start": v(9.47, 10.87) * mm, "mid": v(9.58, 9.5) * mm, "end": v(10.95, 9.53) * mm});
            skArc(sketch, "E20.22.0", {"start": v(18.27, 35.58) * mm, "mid": v(16.67, 35.69) * mm, "end": v(15.51, 34.59) * mm});
            skArc(sketch, "E20.22.1", {"start": v(18.27, 35.58) * mm, "mid": v(18.87, 35.27) * mm, "end": v(19.46, 34.95) * mm});
            skArc(sketch, "E20.22.2", {"start": v(20.2, 32.17) * mm, "mid": v(20.42, 33.72) * mm, "end": v(19.46, 34.95) * mm});
            skLineSegment(sketch, "E20.22.3", {"start": v(8.1, 12.04) * mm, "end": v(20.2, 32.17) * mm});
            skLineSegment(sketch, "E20.22.4", {"start": v(15.51, 34.59) * mm, "end": v(6.33, 12.95) * mm});
            skArc(sketch, "E20.22.5", {"start": v(6.33, 12.95) * mm, "mid": v(6.8, 11.67) * mm, "end": v(8.1, 12.04) * mm});
            skArc(sketch, "E20.23.0", {"start": v(8.44, 39.1) * mm, "mid": v(6.87, 38.79) * mm, "end": v(6.03, 37.42) * mm});
            skArc(sketch, "E20.23.1", {"start": v(8.44, 39.1) * mm, "mid": v(9.1, 38.95) * mm, "end": v(9.75, 38.8) * mm});
            skArc(sketch, "E20.23.2", {"start": v(11.19, 36.3) * mm, "mid": v(11, 37.85) * mm, "end": v(9.75, 38.8) * mm});
            skLineSegment(sketch, "E20.23.3", {"start": v(4.71, 13.73) * mm, "end": v(11.19, 36.3) * mm});
            skLineSegment(sketch, "E20.23.4", {"start": v(6.03, 37.42) * mm, "end": v(2.76, 14.15) * mm});
            skArc(sketch, "E20.23.5", {"start": v(2.76, 14.15) * mm, "mid": v(3.54, 13.03) * mm, "end": v(4.71, 13.73) * mm});
            skSolve(sketch);
        }
        {
            var Q0;
            Q0 = qSketchRegion(id + "F6", true);
            extrude(context, id + "F7", {"entities" : qUnion([Q0]), "operationType" : NewBodyOperationType.REMOVE, "oppositeDirection" : true, "depth" : 25 * mm, "offsetDistance" : 25 * mm});
        }
        {
            var Q0;
            Q0=makeQuery(id+"F3.opExtrude","CAP_FACE",FACE,{"disambiguationData":[OSD([sQuery(id+"F2.wireOp",EDGE,"E1"),sQuery(id+"F2.wireOp",EDGE,"E4"),sQuery(id+"F2.wireOp",EDGE,"E8"),sQuery(id+"F2.wireOp",EDGE,"E9"),sQuery(id+"F2.wireOp",EDGE,"E7.filletArc"),sQuery(id+"F2.wireOp",EDGE,"E6"),sQuery(id+"F2.wireOp",EDGE,"E10.1.0"),sQuery(id+"F2.wireOp",EDGE,"E10.1.1"),sQuery(id+"F2.wireOp",EDGE,"E10.1.2"),sQuery(id+"F2.wireOp",EDGE,"E10.1.3"),sQuery(id+"F2.wireOp",EDGE,"E10.1.4"),sQuery(id+"F2.wireOp",EDGE,"E10.2.0"),sQuery(id+"F2.wireOp",EDGE,"E10.2.1"),sQuery(id+"F2.wireOp",EDGE,"E10.2.2"),sQuery(id+"F2.wireOp",EDGE,"E10.2.3"),sQuery(id+"F2.wireOp",EDGE,"E10.2.4"),sQuery(id+"F2.wireOp",EDGE,"E10.3.0"),sQuery(id+"F2.wireOp",EDGE,"E10.3.1"),sQuery(id+"F2.wireOp",EDGE,"E10.3.2"),sQuery(id+"F2.wireOp",EDGE,"E10.3.3"),sQuery(id+"F2.wireOp",EDGE,"E10.3.4"),sQuery(id+"F2.wireOp",EDGE,"E10.4.0"),sQuery(id+"F2.wireOp",EDGE,"E10.4.1"),sQuery(id+"F2.wireOp",EDGE,"E10.4.2"),sQuery(id+"F2.wireOp",EDGE,"E10.4.3"),sQuery(id+"F2.wireOp",EDGE,"E10.4.4"),sQuery(id+"F2.wireOp",EDGE,"E10.5.0"),sQuery(id+"F2.wireOp",EDGE,"E10.5.1"),sQuery(id+"F2.wireOp",EDGE,"E10.5.2"),sQuery(id+"F2.wireOp",EDGE,"E10.5.3"),sQuery(id+"F2.wireOp",EDGE,"E10.5.4"),sQuery(id+"F2.wireOp",EDGE,"E10.6.0"),sQuery(id+"F2.wireOp",EDGE,"E10.6.1"),sQuery(id+"F2.wireOp",EDGE,"E10.6.2"),sQuery(id+"F2.wireOp",EDGE,"E10.6.3"),sQuery(id+"F2.wireOp",EDGE,"E10.6.4"),sQuery(id+"F2.wireOp",EDGE,"E10.7.0"),sQuery(id+"F2.wireOp",EDGE,"E10.7.1"),sQuery(id+"F2.wireOp",EDGE,"E10.7.2"),sQuery(id+"F2.wireOp",EDGE,"E10.7.3"),sQuery(id+"F2.wireOp",EDGE,"E10.7.4"),sQuery(id+"F2.wireOp",EDGE,"E10.8.0"),sQuery(id+"F2.wireOp",EDGE,"E10.8.1"),sQuery(id+"F2.wireOp",EDGE,"E10.8.2"),sQuery(id+"F2.wireOp",EDGE,"E10.8.3"),sQuery(id+"F2.wireOp",EDGE,"E10.8.4"),sQuery(id+"F2.wireOp",EDGE,"E10.9.0"),sQuery(id+"F2.wireOp",EDGE,"E10.9.1"),sQuery(id+"F2.wireOp",EDGE,"E10.9.2"),sQuery(id+"F2.wireOp",EDGE,"E10.9.3"),sQuery(id+"F2.wireOp",EDGE,"E10.9.4"),sQuery(id+"F2.wireOp",EDGE,"E10.10.0"),sQuery(id+"F2.wireOp",EDGE,"E10.10.1"),sQuery(id+"F2.wireOp",EDGE,"E10.10.2"),sQuery(id+"F2.wireOp",EDGE,"E10.10.3"),sQuery(id+"F2.wireOp",EDGE,"E10.10.4"),sQuery(id+"F2.wireOp",EDGE,"E10.11.0"),sQuery(id+"F2.wireOp",EDGE,"E10.11.1"),sQuery(id+"F2.wireOp",EDGE,"E10.11.2"),sQuery(id+"F2.wireOp",EDGE,"E10.11.3"),sQuery(id+"F2.wireOp",EDGE,"E10.11.4"),sQuery(id+"F2.wireOp",EDGE,"E10.12.0"),sQuery(id+"F2.wireOp",EDGE,"E10.12.1"),sQuery(id+"F2.wireOp",EDGE,"E10.12.2"),sQuery(id+"F2.wireOp",EDGE,"E10.12.3"),sQuery(id+"F2.wireOp",EDGE,"E10.12.4"),sQuery(id+"F2.wireOp",EDGE,"E10.13.0"),sQuery(id+"F2.wireOp",EDGE,"E10.13.1"),sQuery(id+"F2.wireOp",EDGE,"E10.13.2"),sQuery(id+"F2.wireOp",EDGE,"E10.13.3"),sQuery(id+"F2.wireOp",EDGE,"E10.13.4"),sQuery(id+"F2.wireOp",EDGE,"E10.14.0"),sQuery(id+"F2.wireOp",EDGE,"E10.14.1"),sQuery(id+"F2.wireOp",EDGE,"E10.14.2"),sQuery(id+"F2.wireOp",EDGE,"E10.14.3"),sQuery(id+"F2.wireOp",EDGE,"E10.14.4"),sQuery(id+"F2.wireOp",EDGE,"E10.15.0"),sQuery(id+"F2.wireOp",EDGE,"E10.15.1"),sQuery(id+"F2.wireOp",EDGE,"E10.15.2"),sQuery(id+"F2.wireOp",EDGE,"E10.15.3"),sQuery(id+"F2.wireOp",EDGE,"E10.15.4"),sQuery(id+"F2.wireOp",EDGE,"E10.16.0"),sQuery(id+"F2.wireOp",EDGE,"E10.16.1"),sQuery(id+"F2.wireOp",EDGE,"E10.16.2"),sQuery(id+"F2.wireOp",EDGE,"E10.16.3"),sQuery(id+"F2.wireOp",EDGE,"E10.16.4"),sQuery(id+"F2.wireOp",EDGE,"E10.17.0"),sQuery(id+"F2.wireOp",EDGE,"E10.17.1"),sQuery(id+"F2.wireOp",EDGE,"E10.17.2"),sQuery(id+"F2.wireOp",EDGE,"E10.17.3"),sQuery(id+"F2.wireOp",EDGE,"E10.17.4"),sQuery(id+"F2.wireOp",EDGE,"E10.18.0"),sQuery(id+"F2.wireOp",EDGE,"E10.18.1"),sQuery(id+"F2.wireOp",EDGE,"E10.18.2"),sQuery(id+"F2.wireOp",EDGE,"E10.18.3"),sQuery(id+"F2.wireOp",EDGE,"E10.18.4"),sQuery(id+"F2.wireOp",EDGE,"E10.19.0"),sQuery(id+"F2.wireOp",EDGE,"E10.19.1"),sQuery(id+"F2.wireOp",EDGE,"E10.19.2"),sQuery(id+"F2.wireOp",EDGE,"E10.19.3"),sQuery(id+"F2.wireOp",EDGE,"E10.19.4"),sQuery(id+"F2.wireOp",EDGE,"E10.20.0"),sQuery(id+"F2.wireOp",EDGE,"E10.20.1"),sQuery(id+"F2.wireOp",EDGE,"E10.20.2"),sQuery(id+"F2.wireOp",EDGE,"E10.20.3"),sQuery(id+"F2.wireOp",EDGE,"E10.20.4"),sQuery(id+"F2.wireOp",EDGE,"E10.21.0"),sQuery(id+"F2.wireOp",EDGE,"E10.21.1"),sQuery(id+"F2.wireOp",EDGE,"E10.21.2"),sQuery(id+"F2.wireOp",EDGE,"E10.21.3"),sQuery(id+"F2.wireOp",EDGE,"E10.21.4"),sQuery(id+"F2.wireOp",EDGE,"E10.22.0"),sQuery(id+"F2.wireOp",EDGE,"E10.22.1"),sQuery(id+"F2.wireOp",EDGE,"E10.22.2"),sQuery(id+"F2.wireOp",EDGE,"E10.22.3"),sQuery(id+"F2.wireOp",EDGE,"E10.22.4"),sQuery(id+"F2.wireOp",EDGE,"E10.23.0"),sQuery(id+"F2.wireOp",EDGE,"E10.23.1"),sQuery(id+"F2.wireOp",EDGE,"E10.23.2"),sQuery(id+"F2.wireOp",EDGE,"E10.23.3"),sQuery(id+"F2.wireOp",EDGE,"E10.23.4")])],"isStart":false});
            var sketch = newSketch(context, id + "F8", { "sketchPlane" : qUnion([Q0])});
            skEllipse(sketch, "E21", {"center": v(0, 8) * mm, "majorRadius": 3 * mm, "minorRadius": 2.5 * mm, "majorAxis": v(0, -1)});
            skEllipse(sketch, "E22.1.0", {"center": v(-6.93, 4) * mm, "majorRadius": 3 * mm, "minorRadius": 2.5 * mm, "majorAxis": v(0.87, -0.5)});
            skEllipse(sketch, "E22.2.0", {"center": v(-6.93, -4) * mm, "majorRadius": 3 * mm, "minorRadius": 2.5 * mm, "majorAxis": v(0.87, 0.5)});
            skEllipse(sketch, "E22.3.0", {"center": v(0, -8) * mm, "majorRadius": 3 * mm, "minorRadius": 2.5 * mm, "majorAxis": v(0, 1)});
            skEllipse(sketch, "E22.4.0", {"center": v(6.93, -4) * mm, "majorRadius": 3 * mm, "minorRadius": 2.5 * mm, "majorAxis": v(-0.87, 0.5)});
            skEllipse(sketch, "E22.5.0", {"center": v(6.93, 4) * mm, "majorRadius": 3 * mm, "minorRadius": 2.5 * mm, "majorAxis": v(-0.87, -0.5)});
            skPoint(sketch, "E22.center", {"position": v(0, 0) * mm});
            skSolve(sketch);
        }
        {
            var Q0;
            Q0 = qSketchRegion(id + "F8", true);
            extrude(context, id + "F9", {"entities" : qUnion([Q0]), "operationType" : NewBodyOperationType.REMOVE, "oppositeDirection" : true, "depth" : 25 * mm, "offsetDistance" : 25 * mm});
        }
        {
            var Q0;
            Q0=makeQuery(id+"F3.opExtrude","CAP_FACE",FACE,{"disambiguationData":[OSD([sQuery(id+"F2.wireOp",EDGE,"E1"),sQuery(id+"F2.wireOp",EDGE,"E4"),sQuery(id+"F2.wireOp",EDGE,"E8"),sQuery(id+"F2.wireOp",EDGE,"E9"),sQuery(id+"F2.wireOp",EDGE,"E7.filletArc"),sQuery(id+"F2.wireOp",EDGE,"E6"),sQuery(id+"F2.wireOp",EDGE,"E10.1.0"),sQuery(id+"F2.wireOp",EDGE,"E10.1.1"),sQuery(id+"F2.wireOp",EDGE,"E10.1.2"),sQuery(id+"F2.wireOp",EDGE,"E10.1.3"),sQuery(id+"F2.wireOp",EDGE,"E10.1.4"),sQuery(id+"F2.wireOp",EDGE,"E10.2.0"),sQuery(id+"F2.wireOp",EDGE,"E10.2.1"),sQuery(id+"F2.wireOp",EDGE,"E10.2.2"),sQuery(id+"F2.wireOp",EDGE,"E10.2.3"),sQuery(id+"F2.wireOp",EDGE,"E10.2.4"),sQuery(id+"F2.wireOp",EDGE,"E10.3.0"),sQuery(id+"F2.wireOp",EDGE,"E10.3.1"),sQuery(id+"F2.wireOp",EDGE,"E10.3.2"),sQuery(id+"F2.wireOp",EDGE,"E10.3.3"),sQuery(id+"F2.wireOp",EDGE,"E10.3.4"),sQuery(id+"F2.wireOp",EDGE,"E10.4.0"),sQuery(id+"F2.wireOp",EDGE,"E10.4.1"),sQuery(id+"F2.wireOp",EDGE,"E10.4.2"),sQuery(id+"F2.wireOp",EDGE,"E10.4.3"),sQuery(id+"F2.wireOp",EDGE,"E10.4.4"),sQuery(id+"F2.wireOp",EDGE,"E10.5.0"),sQuery(id+"F2.wireOp",EDGE,"E10.5.1"),sQuery(id+"F2.wireOp",EDGE,"E10.5.2"),sQuery(id+"F2.wireOp",EDGE,"E10.5.3"),sQuery(id+"F2.wireOp",EDGE,"E10.5.4"),sQuery(id+"F2.wireOp",EDGE,"E10.6.0"),sQuery(id+"F2.wireOp",EDGE,"E10.6.1"),sQuery(id+"F2.wireOp",EDGE,"E10.6.2"),sQuery(id+"F2.wireOp",EDGE,"E10.6.3"),sQuery(id+"F2.wireOp",EDGE,"E10.6.4"),sQuery(id+"F2.wireOp",EDGE,"E10.7.0"),sQuery(id+"F2.wireOp",EDGE,"E10.7.1"),sQuery(id+"F2.wireOp",EDGE,"E10.7.2"),sQuery(id+"F2.wireOp",EDGE,"E10.7.3"),sQuery(id+"F2.wireOp",EDGE,"E10.7.4"),sQuery(id+"F2.wireOp",EDGE,"E10.8.0"),sQuery(id+"F2.wireOp",EDGE,"E10.8.1"),sQuery(id+"F2.wireOp",EDGE,"E10.8.2"),sQuery(id+"F2.wireOp",EDGE,"E10.8.3"),sQuery(id+"F2.wireOp",EDGE,"E10.8.4"),sQuery(id+"F2.wireOp",EDGE,"E10.9.0"),sQuery(id+"F2.wireOp",EDGE,"E10.9.1"),sQuery(id+"F2.wireOp",EDGE,"E10.9.2"),sQuery(id+"F2.wireOp",EDGE,"E10.9.3"),sQuery(id+"F2.wireOp",EDGE,"E10.9.4"),sQuery(id+"F2.wireOp",EDGE,"E10.10.0"),sQuery(id+"F2.wireOp",EDGE,"E10.10.1"),sQuery(id+"F2.wireOp",EDGE,"E10.10.2"),sQuery(id+"F2.wireOp",EDGE,"E10.10.3"),sQuery(id+"F2.wireOp",EDGE,"E10.10.4"),sQuery(id+"F2.wireOp",EDGE,"E10.11.0"),sQuery(id+"F2.wireOp",EDGE,"E10.11.1"),sQuery(id+"F2.wireOp",EDGE,"E10.11.2"),sQuery(id+"F2.wireOp",EDGE,"E10.11.3"),sQuery(id+"F2.wireOp",EDGE,"E10.11.4"),sQuery(id+"F2.wireOp",EDGE,"E10.12.0"),sQuery(id+"F2.wireOp",EDGE,"E10.12.1"),sQuery(id+"F2.wireOp",EDGE,"E10.12.2"),sQuery(id+"F2.wireOp",EDGE,"E10.12.3"),sQuery(id+"F2.wireOp",EDGE,"E10.12.4"),sQuery(id+"F2.wireOp",EDGE,"E10.13.0"),sQuery(id+"F2.wireOp",EDGE,"E10.13.1"),sQuery(id+"F2.wireOp",EDGE,"E10.13.2"),sQuery(id+"F2.wireOp",EDGE,"E10.13.3"),sQuery(id+"F2.wireOp",EDGE,"E10.13.4"),sQuery(id+"F2.wireOp",EDGE,"E10.14.0"),sQuery(id+"F2.wireOp",EDGE,"E10.14.1"),sQuery(id+"F2.wireOp",EDGE,"E10.14.2"),sQuery(id+"F2.wireOp",EDGE,"E10.14.3"),sQuery(id+"F2.wireOp",EDGE,"E10.14.4"),sQuery(id+"F2.wireOp",EDGE,"E10.15.0"),sQuery(id+"F2.wireOp",EDGE,"E10.15.1"),sQuery(id+"F2.wireOp",EDGE,"E10.15.2"),sQuery(id+"F2.wireOp",EDGE,"E10.15.3"),sQuery(id+"F2.wireOp",EDGE,"E10.15.4"),sQuery(id+"F2.wireOp",EDGE,"E10.16.0"),sQuery(id+"F2.wireOp",EDGE,"E10.16.1"),sQuery(id+"F2.wireOp",EDGE,"E10.16.2"),sQuery(id+"F2.wireOp",EDGE,"E10.16.3"),sQuery(id+"F2.wireOp",EDGE,"E10.16.4"),sQuery(id+"F2.wireOp",EDGE,"E10.17.0"),sQuery(id+"F2.wireOp",EDGE,"E10.17.1"),sQuery(id+"F2.wireOp",EDGE,"E10.17.2"),sQuery(id+"F2.wireOp",EDGE,"E10.17.3"),sQuery(id+"F2.wireOp",EDGE,"E10.17.4"),sQuery(id+"F2.wireOp",EDGE,"E10.18.0"),sQuery(id+"F2.wireOp",EDGE,"E10.18.1"),sQuery(id+"F2.wireOp",EDGE,"E10.18.2"),sQuery(id+"F2.wireOp",EDGE,"E10.18.3"),sQuery(id+"F2.wireOp",EDGE,"E10.18.4"),sQuery(id+"F2.wireOp",EDGE,"E10.19.0"),sQuery(id+"F2.wireOp",EDGE,"E10.19.1"),sQuery(id+"F2.wireOp",EDGE,"E10.19.2"),sQuery(id+"F2.wireOp",EDGE,"E10.19.3"),sQuery(id+"F2.wireOp",EDGE,"E10.19.4"),sQuery(id+"F2.wireOp",EDGE,"E10.20.0"),sQuery(id+"F2.wireOp",EDGE,"E10.20.1"),sQuery(id+"F2.wireOp",EDGE,"E10.20.2"),sQuery(id+"F2.wireOp",EDGE,"E10.20.3"),sQuery(id+"F2.wireOp",EDGE,"E10.20.4"),sQuery(id+"F2.wireOp",EDGE,"E10.21.0"),sQuery(id+"F2.wireOp",EDGE,"E10.21.1"),sQuery(id+"F2.wireOp",EDGE,"E10.21.2"),sQuery(id+"F2.wireOp",EDGE,"E10.21.3"),sQuery(id+"F2.wireOp",EDGE,"E10.21.4"),sQuery(id+"F2.wireOp",EDGE,"E10.22.0"),sQuery(id+"F2.wireOp",EDGE,"E10.22.1"),sQuery(id+"F2.wireOp",EDGE,"E10.22.2"),sQuery(id+"F2.wireOp",EDGE,"E10.22.3"),sQuery(id+"F2.wireOp",EDGE,"E10.22.4"),sQuery(id+"F2.wireOp",EDGE,"E10.23.0"),sQuery(id+"F2.wireOp",EDGE,"E10.23.1"),sQuery(id+"F2.wireOp",EDGE,"E10.23.2"),sQuery(id+"F2.wireOp",EDGE,"E10.23.3"),sQuery(id+"F2.wireOp",EDGE,"E10.23.4")])],"isStart":false});
            var sketch = newSketch(context, id + "F10", { "sketchPlane" : qUnion([Q0])});
            skEllipse(sketch, "E23", {"center": v(-5.68, 43.13) * mm, "majorRadius": 3 * mm, "minorRadius": 1.5 * mm, "majorAxis": v(-0.38, -0.92)});
            skLineSegment(sketch, "E24", {"start": v(0, 0) * mm, "end": v(-5.68, 43.13) * mm, "construction": true});
            skLineSegment(sketch, "E25", {"start": v(-4.53, 45.9) * mm, "end": v(-6.83, 40.36) * mm, "construction": true});
            skEllipse(sketch, "E26.1.0", {"center": v(-16.65, 40.19) * mm, "majorRadius": 3 * mm, "minorRadius": 1.5 * mm, "majorAxis": v(-0.13, -1)});
            skEllipse(sketch, "E26.2.0", {"center": v(-26.48, 34.51) * mm, "majorRadius": 3 * mm, "minorRadius": 1.5 * mm, "majorAxis": v(0.13, -1)});
            skEllipse(sketch, "E26.3.0", {"center": v(-34.51, 26.48) * mm, "majorRadius": 3 * mm, "minorRadius": 1.5 * mm, "majorAxis": v(0.38, -0.92)});
            skEllipse(sketch, "E26.4.0", {"center": v(-40.19, 16.65) * mm, "majorRadius": 3 * mm, "minorRadius": 1.5 * mm, "majorAxis": v(0.6, -0.8)});
            skEllipse(sketch, "E26.5.0", {"center": v(-43.13, 5.68) * mm, "majorRadius": 3 * mm, "minorRadius": 1.5 * mm, "majorAxis": v(0.8, -0.6)});
            skEllipse(sketch, "E26.6.0", {"center": v(-43.13, -5.68) * mm, "majorRadius": 3 * mm, "minorRadius": 1.5 * mm, "majorAxis": v(0.92, -0.38)});
            skEllipse(sketch, "E26.7.0", {"center": v(-40.19, -16.65) * mm, "majorRadius": 3 * mm, "minorRadius": 1.5 * mm, "majorAxis": v(1, -0.13)});
            skEllipse(sketch, "E26.8.0", {"center": v(-34.51, -26.48) * mm, "majorRadius": 3 * mm, "minorRadius": 1.5 * mm, "majorAxis": v(1, 0.13)});
            skEllipse(sketch, "E26.9.0", {"center": v(-26.48, -34.51) * mm, "majorRadius": 3 * mm, "minorRadius": 1.5 * mm, "majorAxis": v(0.92, 0.38)});
            skEllipse(sketch, "E26.10.0", {"center": v(-16.65, -40.19) * mm, "majorRadius": 3 * mm, "minorRadius": 1.5 * mm, "majorAxis": v(0.8, 0.6)});
            skEllipse(sketch, "E26.11.0", {"center": v(-5.68, -43.13) * mm, "majorRadius": 3 * mm, "minorRadius": 1.5 * mm, "majorAxis": v(0.6, 0.8)});
            skEllipse(sketch, "E26.12.0", {"center": v(5.68, -43.13) * mm, "majorRadius": 3 * mm, "minorRadius": 1.5 * mm, "majorAxis": v(0.38, 0.92)});
            skEllipse(sketch, "E26.13.0", {"center": v(16.65, -40.19) * mm, "majorRadius": 3 * mm, "minorRadius": 1.5 * mm, "majorAxis": v(0.13, 1)});
            skEllipse(sketch, "E26.14.0", {"center": v(26.48, -34.51) * mm, "majorRadius": 3 * mm, "minorRadius": 1.5 * mm, "majorAxis": v(-0.13, 1)});
            skEllipse(sketch, "E26.15.0", {"center": v(34.51, -26.48) * mm, "majorRadius": 3 * mm, "minorRadius": 1.5 * mm, "majorAxis": v(-0.38, 0.92)});
            skEllipse(sketch, "E26.16.0", {"center": v(40.19, -16.65) * mm, "majorRadius": 3 * mm, "minorRadius": 1.5 * mm, "majorAxis": v(-0.6, 0.8)});
            skEllipse(sketch, "E26.17.0", {"center": v(43.13, -5.68) * mm, "majorRadius": 3 * mm, "minorRadius": 1.5 * mm, "majorAxis": v(-0.8, 0.6)});
            skEllipse(sketch, "E26.18.0", {"center": v(43.13, 5.68) * mm, "majorRadius": 3 * mm, "minorRadius": 1.5 * mm, "majorAxis": v(-0.92, 0.38)});
            skEllipse(sketch, "E26.19.0", {"center": v(40.19, 16.65) * mm, "majorRadius": 3 * mm, "minorRadius": 1.5 * mm, "majorAxis": v(-1, 0.13)});
            skEllipse(sketch, "E26.20.0", {"center": v(34.51, 26.48) * mm, "majorRadius": 3 * mm, "minorRadius": 1.5 * mm, "majorAxis": v(-1, -0.13)});
            skEllipse(sketch, "E26.21.0", {"center": v(26.48, 34.51) * mm, "majorRadius": 3 * mm, "minorRadius": 1.5 * mm, "majorAxis": v(-0.92, -0.38)});
            skEllipse(sketch, "E26.22.0", {"center": v(16.65, 40.19) * mm, "majorRadius": 3 * mm, "minorRadius": 1.5 * mm, "majorAxis": v(-0.8, -0.6)});
            skEllipse(sketch, "E26.23.0", {"center": v(5.68, 43.13) * mm, "majorRadius": 3 * mm, "minorRadius": 1.5 * mm, "majorAxis": v(-0.6, -0.8)});
            skPoint(sketch, "E26.center", {"position": v(0, 0) * mm});
            skSolve(sketch);
        }
        {
            var Q0;
            Q0 = qSketchRegion(id + "F10", true);
            extrude(context, id + "F11", {"entities" : qUnion([Q0]), "operationType" : NewBodyOperationType.REMOVE, "oppositeDirection" : true, "depth" : 25 * mm, "offsetDistance" : 25 * mm});
        }
    });
